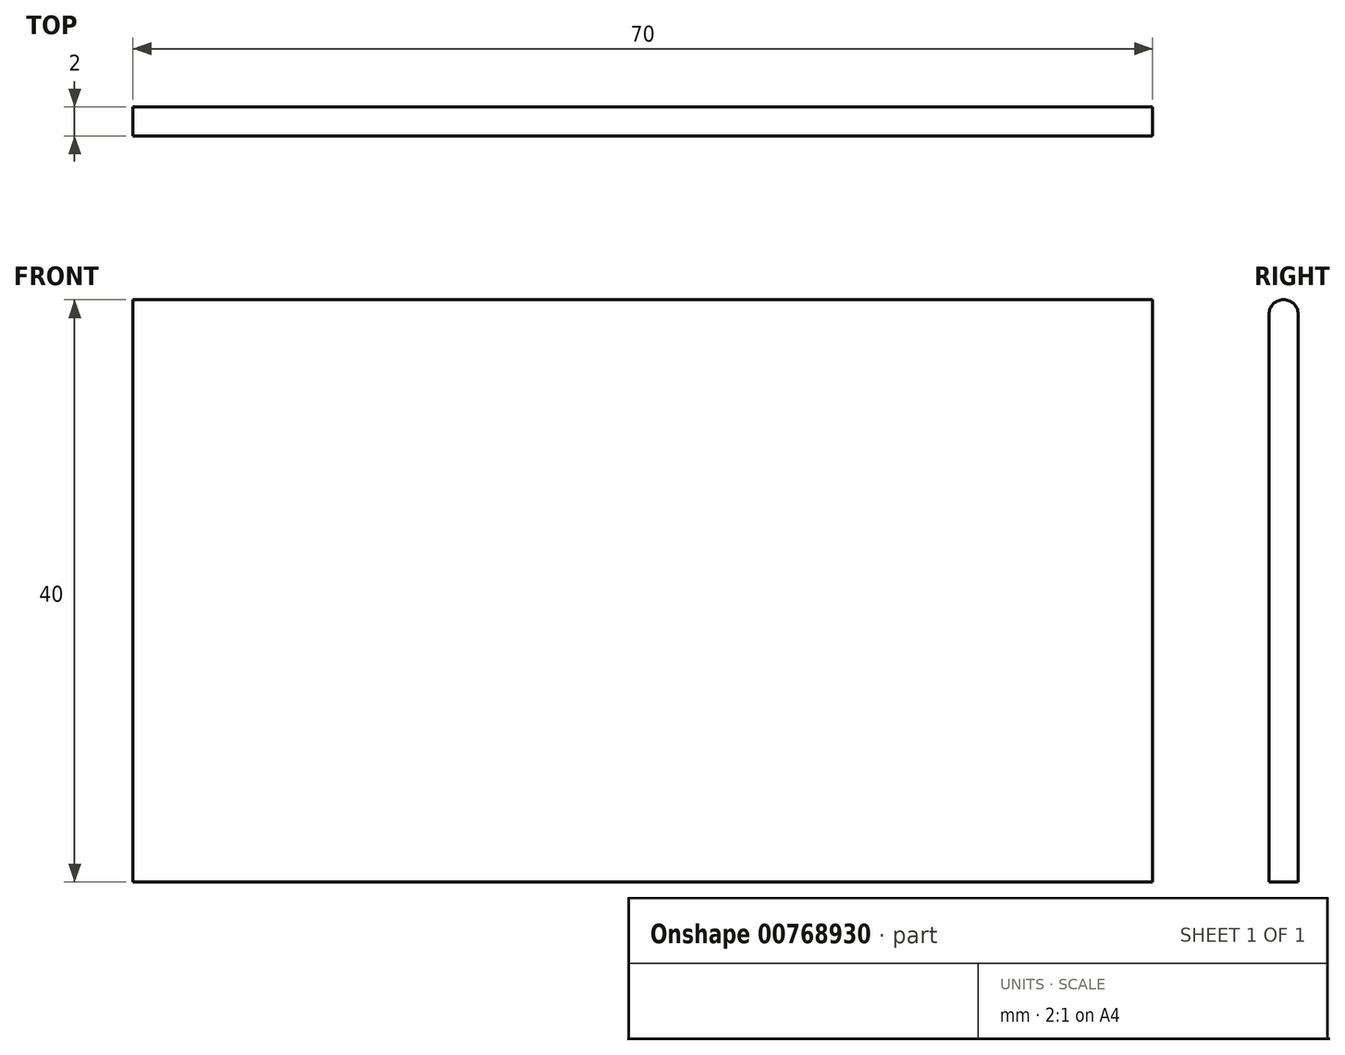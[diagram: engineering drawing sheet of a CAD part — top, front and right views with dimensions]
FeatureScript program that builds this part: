
annotation { "Feature Type Name" : "Feature", "Feature Type Description" : "" }
export const myFeature = defineFeature(function(context is Context, id is Id, definition is map)
    precondition{}
    {
        {
            var Q0;
            Q0=qCreatedBy(makeId("Top.planeOp"),FACE);
            var sketch = newSketch(context, id + "F0", { "sketchPlane" : qUnion([Q0])});
            skLineSegment(sketch, "E0.bottom", {"start": v(0, 0) * mm, "end": v(92.5, 0) * mm});
            skLineSegment(sketch, "E0.top", {"start": v(0, 20) * mm, "end": v(92.5, 20) * mm});
            skLineSegment(sketch, "E0.left", {"start": v(0, 0) * mm, "end": v(0, 20) * mm});
            skLineSegment(sketch, "E0.right", {"start": v(92.5, 0) * mm, "end": v(92.5, 20) * mm});
            skSolve(sketch);
        }
        {
            var Q0;
            Q0 = qSketchRegion(id + "F0", true);
            extrude(context, id + "F1", {"entities" : qUnion([Q0]), "depth" : 1.4 * mm, "offsetDistance" : 25 * mm});
        }
        {
            var Q0;
            Q0=makeQuery(id+"F1.opExtrude","CAP_FACE",FACE,{"disambiguationData":[OSD([sQuery(id+"F0.wireOp",EDGE,"E0.bottom"),sQuery(id+"F0.wireOp",EDGE,"E0.top"),sQuery(id+"F0.wireOp",EDGE,"E0.left"),sQuery(id+"F0.wireOp",EDGE,"E0.right")])],"isStart":false});
            var sketch = newSketch(context, id + "F2", { "sketchPlane" : qUnion([Q0])});
            skLineSegment(sketch, "E1", {"start": v(0, 20) * mm, "end": v(0, 17.6) * mm});
            skLineSegment(sketch, "E2.bottom", {"start": v(0, 17.6) * mm, "end": v(2, 17.6) * mm});
            skLineSegment(sketch, "E2.top", {"start": v(0, 15.6) * mm, "end": v(2, 15.6) * mm});
            skLineSegment(sketch, "E2.left", {"start": v(0, 17.6) * mm, "end": v(0, 15.6) * mm});
            skLineSegment(sketch, "E2.right", {"start": v(2, 17.6) * mm, "end": v(2, 15.6) * mm});
            skLineSegment(sketch, "E3", {"start": v(0, 15.6) * mm, "end": v(0, 13.2) * mm});
            skLineSegment(sketch, "E4.bottom", {"start": v(0, 13.2) * mm, "end": v(2, 13.2) * mm});
            skLineSegment(sketch, "E4.top", {"start": v(0, 11.2) * mm, "end": v(2, 11.2) * mm});
            skLineSegment(sketch, "E4.left", {"start": v(0, 13.2) * mm, "end": v(0, 11.2) * mm});
            skLineSegment(sketch, "E4.right", {"start": v(2, 13.2) * mm, "end": v(2, 11.2) * mm});
            skLineSegment(sketch, "E5", {"start": v(0, 11.2) * mm, "end": v(0, 8.8) * mm});
            skLineSegment(sketch, "E6.bottom", {"start": v(0, 8.8) * mm, "end": v(2, 8.8) * mm});
            skLineSegment(sketch, "E6.top", {"start": v(0, 6.8) * mm, "end": v(2, 6.8) * mm});
            skLineSegment(sketch, "E6.left", {"start": v(0, 8.8) * mm, "end": v(0, 6.8) * mm});
            skLineSegment(sketch, "E6.right", {"start": v(2, 8.8) * mm, "end": v(2, 6.8) * mm});
            skLineSegment(sketch, "E7", {"start": v(0, 6.8) * mm, "end": v(0, 4.4) * mm});
            skLineSegment(sketch, "E8.bottom", {"start": v(0, 4.4) * mm, "end": v(2, 4.4) * mm});
            skLineSegment(sketch, "E8.top", {"start": v(0, 2.4) * mm, "end": v(2, 2.4) * mm});
            skLineSegment(sketch, "E8.left", {"start": v(0, 4.4) * mm, "end": v(0, 2.4) * mm});
            skLineSegment(sketch, "E8.right", {"start": v(2, 4.4) * mm, "end": v(2, 2.4) * mm});
            skSolve(sketch);
        }
        {
            var Q0;
            Q0 = qSketchRegion(id + "F2", true);
            extrude(context, id + "F3", {"entities" : qUnion([Q0]), "operationType" : NewBodyOperationType.REMOVE, "oppositeDirection" : true, "depth" : 25 * mm, "offsetDistance" : 25 * mm});
        }
        {
            var Q0;
            Q0=makeQuery(id+"F3.boolean.opBoolean","COPY",EDGE,{"derivedFrom":makeQuery(id+"F3.opExtrude","SWEPT_EDGE",EDGE,{"disambiguationData":[OSD([sQuery(id+"F2.wireOp",EDGE,"E2.top"),sQuery(id+"F2.wireOp",EDGE,"E2.right")])]})});
            var Q1;
            Q1=makeQuery(id+"F3.boolean.opBoolean","COPY",EDGE,{"derivedFrom":makeQuery(id+"F3.opExtrude","SWEPT_EDGE",EDGE,{"disambiguationData":[OSD([sQuery(id+"F2.wireOp",EDGE,"E2.bottom"),sQuery(id+"F2.wireOp",EDGE,"E2.right")])]})});
            var Q2;
            Q2=makeQuery(id+"F3.boolean.opBoolean","COPY",EDGE,{"derivedFrom":makeQuery(id+"F3.opExtrude","SWEPT_EDGE",EDGE,{"disambiguationData":[OSD([sQuery(id+"F2.wireOp",EDGE,"E4.bottom"),sQuery(id+"F2.wireOp",EDGE,"E4.right")])]})});
            var Q3;
            Q3=makeQuery(id+"F3.boolean.opBoolean","COPY",EDGE,{"derivedFrom":makeQuery(id+"F3.opExtrude","SWEPT_EDGE",EDGE,{"disambiguationData":[OSD([sQuery(id+"F2.wireOp",EDGE,"E4.top"),sQuery(id+"F2.wireOp",EDGE,"E4.right")])]})});
            var Q4;
            Q4=makeQuery(id+"F3.boolean.opBoolean","COPY",EDGE,{"derivedFrom":makeQuery(id+"F3.opExtrude","SWEPT_EDGE",EDGE,{"disambiguationData":[OSD([sQuery(id+"F2.wireOp",EDGE,"E6.top"),sQuery(id+"F2.wireOp",EDGE,"E6.right")])]})});
            var Q5;
            Q5=makeQuery(id+"F3.boolean.opBoolean","COPY",EDGE,{"derivedFrom":makeQuery(id+"F3.opExtrude","SWEPT_EDGE",EDGE,{"disambiguationData":[OSD([sQuery(id+"F2.wireOp",EDGE,"E6.bottom"),sQuery(id+"F2.wireOp",EDGE,"E6.right")])]})});
            var Q6;
            Q6=makeQuery(id+"F3.boolean.opBoolean","COPY",EDGE,{"derivedFrom":makeQuery(id+"F3.opExtrude","SWEPT_EDGE",EDGE,{"disambiguationData":[OSD([sQuery(id+"F2.wireOp",EDGE,"E8.bottom"),sQuery(id+"F2.wireOp",EDGE,"E8.right")])]})});
            var Q7;
            Q7=makeQuery(id+"F3.boolean.opBoolean","COPY",EDGE,{"derivedFrom":makeQuery(id+"F3.opExtrude","SWEPT_EDGE",EDGE,{"disambiguationData":[OSD([sQuery(id+"F2.wireOp",EDGE,"E8.top"),sQuery(id+"F2.wireOp",EDGE,"E8.right")])]})});
            fillet(context, id + "F4", {"entities" : qUnion([Q0, Q1, Q2, Q3, Q4, Q5, Q6, Q7]), "radius" : 0.8 * mm, "tangentPropagation" : true, "allowEdgeOverflow" : false});
        }
        {
            var Q0;
            Q0=makeQuery(id+"F1.opExtrude","SWEPT_BODY",BODY,{"disambiguationData":[OSD([sQuery(id+"F0.wireOp",EDGE,"E0.bottom"),sQuery(id+"F0.wireOp",EDGE,"E0.top"),sQuery(id+"F0.wireOp",EDGE,"E0.left"),sQuery(id+"F0.wireOp",EDGE,"E0.right")])]});
            deleteBodies(context, id + "F5", {"entities" : qUnion([Q0])});
        }
        {
            var Q0;
            Q0=qCreatedBy(makeId("Front.planeOp"),FACE);
            var sketch = newSketch(context, id + "F6", { "sketchPlane" : qUnion([Q0])});
            skLineSegment(sketch, "E9.bottom", {"start": v(0, 0) * mm, "end": v(70, 0) * mm});
            skLineSegment(sketch, "E9.top", {"start": v(0, 40) * mm, "end": v(70, 40) * mm});
            skLineSegment(sketch, "E9.left", {"start": v(0, 0) * mm, "end": v(0, 40) * mm});
            skLineSegment(sketch, "E9.right", {"start": v(70, 0) * mm, "end": v(70, 40) * mm});
            skSolve(sketch);
        }
        {
            var Q0;
            Q0 = qSketchRegion(id + "F6", true);
            extrude(context, id + "F7", {"entities" : qUnion([Q0]), "depth" : 2 * mm, "offsetDistance" : 25 * mm});
        }
        {
            var Q0;
            Q0=makeQuery(id+"F7.opExtrude","CAP_EDGE",EDGE,{"disambiguationData":[OSD([sQuery(id+"F6.wireOp",EDGE,"E9.top")])],"isStart":false});
            var Q1;
            Q1=makeQuery(id+"F7.opExtrude","CAP_EDGE",EDGE,{"disambiguationData":[OSD([sQuery(id+"F6.wireOp",EDGE,"E9.top")])],"isStart":true});
            fillet(context, id + "F8", {"entities" : qUnion([Q0, Q1]), "radius" : 1 * mm, "tangentPropagation" : true, "allowEdgeOverflow" : false});
        }
    });
